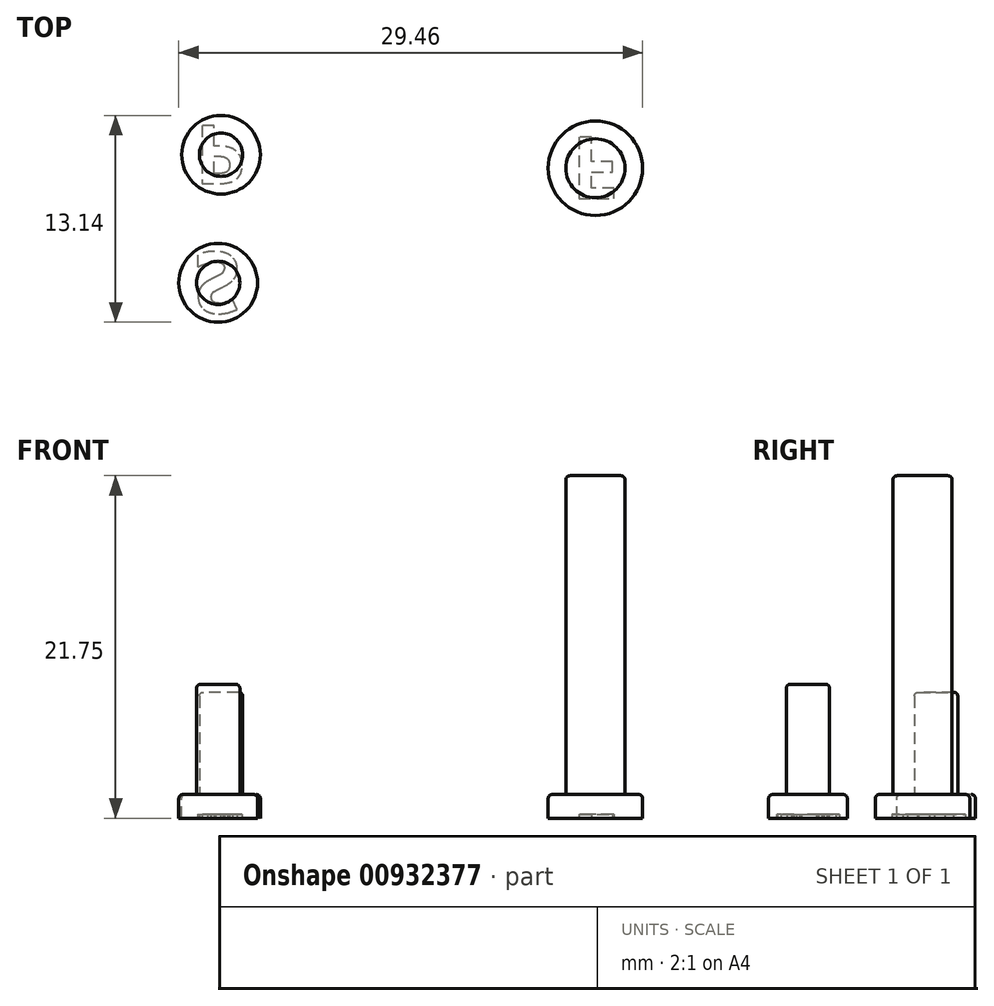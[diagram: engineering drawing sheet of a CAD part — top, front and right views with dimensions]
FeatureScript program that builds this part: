
annotation { "Feature Type Name" : "Feature", "Feature Type Description" : "" }
export const myFeature = defineFeature(function(context is Context, id is Id, definition is map)
    precondition{}
    {
        {
            var Q0;
            Q0=qCreatedBy(makeId("Top.planeOp"),FACE);
            var sketch = newSketch(context, id + "F0", { "sketchPlane" : qUnion([Q0])});
            skCircle(sketch, "E0", {"center": v(-13.67, -9.02) * mm, "radius": 1.38 * mm});
            skCircle(sketch, "E1", {"center": v(-13.67, -9.02) * mm, "radius": 2.5 * mm});
            skSolve(sketch);
        }
        {
            var Q0;
            Q0=makeQuery(id+"F0.imprint","IMPRINT",FACE,{"disambiguationData":[TD([[makeQuery(id+"F0.imprint","IMPRINT",EDGE,{"derivedFrom":sQuery(id+"F0.wireOp",EDGE,"E0")}),1.0]])]});
            extrude(context, id + "F1", {"entities" : qUnion([Q0]), "depth" : 7 * mm, "offsetDistance" : 25 * mm});
        }
        {
            var Q0;
            Q0=makeQuery(id+"F0.imprint","IMPRINT",FACE,{"disambiguationData":[TD([[makeQuery(id+"F0.imprint","IMPRINT",EDGE,{"derivedFrom":sQuery(id+"F0.wireOp",EDGE,"E0")}),-1.0]])]});
            var Q1;
            Q1=makeQuery(id+"F0.imprint","IMPRINT",FACE,{"disambiguationData":[TD([[makeQuery(id+"F0.imprint","IMPRINT",EDGE,{"derivedFrom":sQuery(id+"F0.wireOp",EDGE,"E0")}),1.0]])]});
            extrude(context, id + "F2", {"entities" : qUnion([Q0, Q1]), "operationType" : NewBodyOperationType.ADD, "oppositeDirection" : true, "depth" : 1.5 * mm, "offsetDistance" : 25 * mm});
        }
        {
            var Q0;
            Q0=makeQuery(id+"F2.opExtrude","CAP_FACE",FACE,{"disambiguationData":[OSD([sQuery(id+"F0.wireOp",EDGE,"E1")])],"isStart":false});
            var sketch = newSketch(context, id + "F3", { "sketchPlane" : qUnion([Q0])});
            skText(sketch, "E2", { "text": "S", "fontName": "OpenSans-Bold.ttf"});
            const initialGuessF3  = {"E2": [-0.01523, 0.00707, 1, 0, 0.0039]};
            skSetInitialGuess(sketch, initialGuessF3);
            skSolve(sketch);
        }
        {
            var Q0;
            Q0=qCreatedBy(makeId("Top.planeOp"),FACE);
            var sketch = newSketch(context, id + "F4", { "sketchPlane" : qUnion([Q0])});
            skCircle(sketch, "E3", {"center": v(-13.49, -0.88) * mm, "radius": 2.5 * mm});
            skCircle(sketch, "E4", {"center": v(-13.49, -0.88) * mm, "radius": 1.38 * mm});
            skSolve(sketch);
        }
        {
            var Q0;
            Q0=makeQuery(id+"F4.imprint","IMPRINT",FACE,{"disambiguationData":[TD([[makeQuery(id+"F4.imprint","IMPRINT",EDGE,{"derivedFrom":sQuery(id+"F4.wireOp",EDGE,"E4")}),1.0]])]});
            extrude(context, id + "F5", {"entities" : qUnion([Q0]), "depth" : 6.5 * mm, "offsetDistance" : 25 * mm});
        }
        {
            var Q0;
            Q0=makeQuery(id+"F4.imprint","IMPRINT",FACE,{"disambiguationData":[TD([[makeQuery(id+"F4.imprint","IMPRINT",EDGE,{"derivedFrom":sQuery(id+"F4.wireOp",EDGE,"E4")}),1.0]])]});
            var Q1;
            Q1=makeQuery(id+"F4.imprint","IMPRINT",FACE,{"disambiguationData":[TD([[makeQuery(id+"F4.imprint","IMPRINT",EDGE,{"derivedFrom":sQuery(id+"F4.wireOp",EDGE,"E3")}),1.0]])]});
            extrude(context, id + "F6", {"entities" : qUnion([Q0, Q1]), "operationType" : NewBodyOperationType.ADD, "oppositeDirection" : true, "depth" : 1.5 * mm, "offsetDistance" : 25 * mm});
        }
        {
            var Q0;
            Q0=makeQuery(id+"F6.opExtrude","CAP_FACE",FACE,{"disambiguationData":[OSD([sQuery(id+"F4.wireOp",EDGE,"E3")])],"isStart":false});
            var sketch = newSketch(context, id + "F7", { "sketchPlane" : qUnion([Q0])});
            skText(sketch, "E5", { "text": "P", "fontName": "OpenSans-Bold.ttf"});
            const initialGuessF7  = {"E5": [-0.01516, -0.00098, 1, 0, 0.00372]};
            skSetInitialGuess(sketch, initialGuessF7);
            skSolve(sketch);
        }
        {
            var Q0;
            Q0=qCreatedBy(makeId("Top.planeOp"),FACE);
            var sketch = newSketch(context, id + "F8", { "sketchPlane" : qUnion([Q0])});
            skCircle(sketch, "E6", {"center": v(10.3, -1.74) * mm, "radius": 3 * mm});
            skCircle(sketch, "E7", {"center": v(10.3, -1.74) * mm, "radius": 1.88 * mm});
            skSolve(sketch);
        }
        {
            var Q0;
            Q0=makeQuery(id+"F8.imprint","IMPRINT",FACE,{"disambiguationData":[TD([[makeQuery(id+"F8.imprint","IMPRINT",EDGE,{"derivedFrom":sQuery(id+"F8.wireOp",EDGE,"E7")}),1.0]])]});
            extrude(context, id + "F9", {"entities" : qUnion([Q0]), "depth" : (15.25 + 5) * mm, "offsetDistance" : 25 * mm});
        }
        {
            var Q0;
            Q0=makeQuery(id+"F8.imprint","IMPRINT",FACE,{"disambiguationData":[TD([[makeQuery(id+"F8.imprint","IMPRINT",EDGE,{"derivedFrom":sQuery(id+"F8.wireOp",EDGE,"E7")}),1.0]])]});
            var Q1;
            Q1=makeQuery(id+"F8.imprint","IMPRINT",FACE,{"disambiguationData":[TD([[makeQuery(id+"F8.imprint","IMPRINT",EDGE,{"derivedFrom":sQuery(id+"F8.wireOp",EDGE,"E6")}),1.0]])]});
            extrude(context, id + "F10", {"entities" : qUnion([Q0, Q1]), "operationType" : NewBodyOperationType.ADD, "oppositeDirection" : true, "depth" : 1.5 * mm, "offsetDistance" : 25 * mm});
        }
        {
            var Q0;
            Q0=makeQuery(id+"F10.opExtrude","CAP_FACE",FACE,{"disambiguationData":[OSD([sQuery(id+"F8.wireOp",EDGE,"E6")])],"isStart":false});
            var sketch = newSketch(context, id + "F11", { "sketchPlane" : qUnion([Q0])});
            skText(sketch, "E8", { "text": "F", "fontName": "OpenSans-Bold.ttf"});
            const initialGuessF11  = {"E8": [0.00875, -0.00023, 1, 0, 0.00394]};
            skSetInitialGuess(sketch, initialGuessF11);
            skSolve(sketch);
        }
        {
            var Q0;
            Q0 = qSketchRegion(id + "F11", true);
            var Q1;
            Q1 = qSketchRegion(id + "F7", true);
            var Q2;
            Q2 = qSketchRegion(id + "F3", true);
            extrude(context, id + "F12", {"entities" : qUnion([Q0, Q1, Q2]), "operationType" : NewBodyOperationType.REMOVE, "oppositeDirection" : true, "depth" : .25 * mm, "offsetDistance" : 25 * mm});
        }
        {
            var Q0;
            Q0=makeQuery(id+"F2.opExtrude","CAP_EDGE",EDGE,{"disambiguationData":[OSD([sQuery(id+"F0.wireOp",EDGE,"E1")])],"isStart":true});
            var Q1;
            Q1=makeQuery(id+"F6.opExtrude","CAP_EDGE",EDGE,{"disambiguationData":[OSD([sQuery(id+"F4.wireOp",EDGE,"E3")])],"isStart":true});
            var Q2;
            Q2=makeQuery(id+"F10.opExtrude","CAP_EDGE",EDGE,{"disambiguationData":[OSD([sQuery(id+"F8.wireOp",EDGE,"E6")])],"isStart":true});
            var Q3;
            Q3=makeQuery(id+"F9.opExtrude","CAP_EDGE",EDGE,{"disambiguationData":[OSD([sQuery(id+"F8.wireOp",EDGE,"E7")])],"isStart":false});
            var Q4;
            Q4=makeQuery(id+"F5.opExtrude","CAP_EDGE",EDGE,{"disambiguationData":[OSD([sQuery(id+"F4.wireOp",EDGE,"E4")])],"isStart":false});
            var Q5;
            Q5=makeQuery(id+"F1.opExtrude","CAP_EDGE",EDGE,{"disambiguationData":[OSD([sQuery(id+"F0.wireOp",EDGE,"E0")])],"isStart":false});
            fillet(context, id + "F13", {"entities" : qUnion([Q0, Q1, Q2, Q3, Q4, Q5]), "radius" : .25 * mm, "tangentPropagation" : true, "allowEdgeOverflow" : false});
        }
    });
